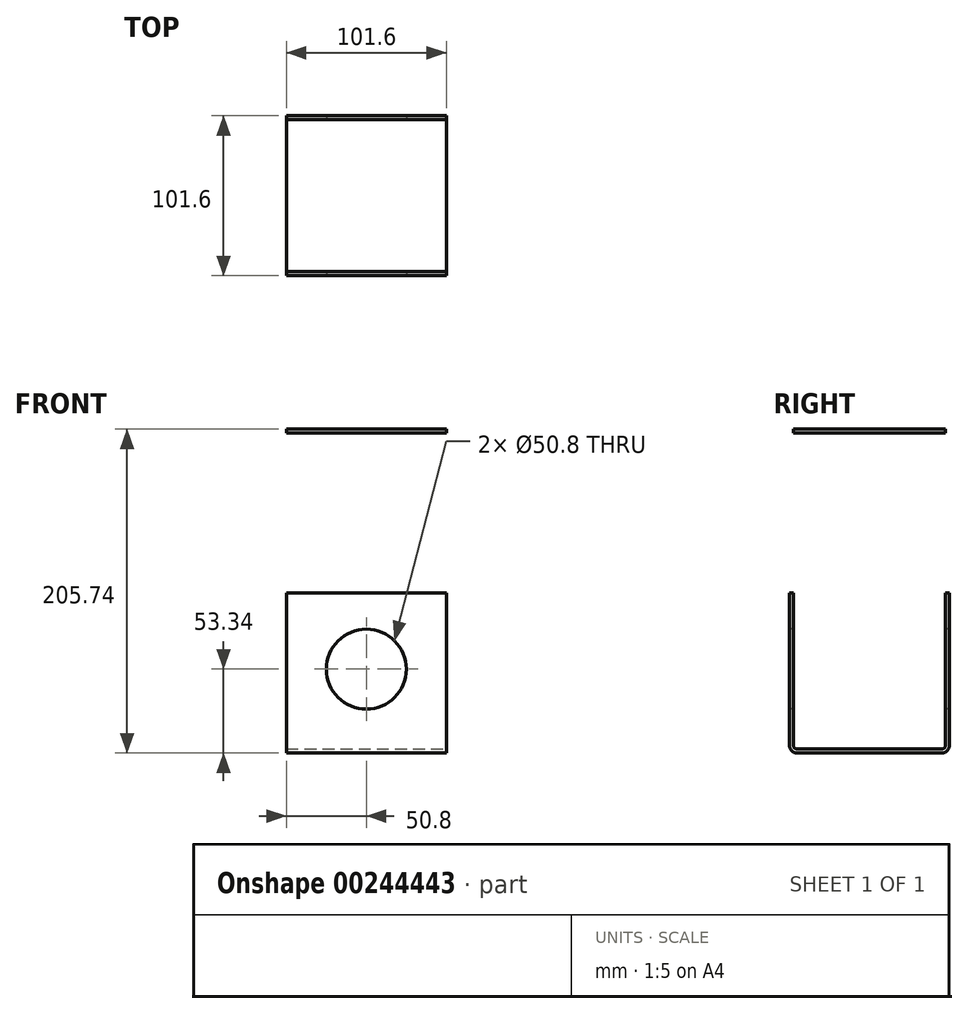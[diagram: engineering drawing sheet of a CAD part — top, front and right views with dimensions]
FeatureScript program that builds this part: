
annotation { "Feature Type Name" : "Feature", "Feature Type Description" : "" }
export const myFeature = defineFeature(function(context is Context, id is Id, definition is map)
    precondition{}
    {
        {
            var Q0;
            Q0=qCreatedBy(makeId("Top.planeOp"),FACE);
            var sketch = newSketch(context, id + "F0", { "sketchPlane" : qUnion([Q0])});
            skLineSegment(sketch, "E0.bottom", {"start": v(50.8, 50.8) * mm, "end": v(-50.8, 50.8) * mm});
            skLineSegment(sketch, "E0.top", {"start": v(50.8, -50.8) * mm, "end": v(-50.8, -50.8) * mm});
            skLineSegment(sketch, "E0.left", {"start": v(50.8, 50.8) * mm, "end": v(50.8, -50.8) * mm});
            skLineSegment(sketch, "E0.right", {"start": v(-50.8, 50.8) * mm, "end": v(-50.8, -50.8) * mm});
            skPoint(sketch, "E0.middle", {"position": v(0, 0) * mm});
            skSolve(sketch);
        }
        {
            var Q0;
            Q0 = qSketchRegion(id + "F0", true);
            extrude(context, id + "F1", {"entities" : qUnion([Q0]), "depth" : 101.6 * mm});
        }
        {
            var Q0;
            Q0=makeQuery(id+"F1.opExtrude","CAP_EDGE",EDGE,{"disambiguationData":[OSD([sQuery(id+"F0.wireOp",EDGE,"E0.top")])],"isStart":true});
            var Q1;
            Q1=makeQuery(id+"F1.opExtrude","CAP_EDGE",EDGE,{"disambiguationData":[OSD([sQuery(id+"F0.wireOp",EDGE,"E0.bottom")])],"isStart":true});
            fillet(context, id + "F2", {"entities" : qUnion([Q0, Q1]), "radius" : 5.08 * mm, "tangentPropagation" : true, "allowEdgeOverflow" : false});
        }
        {
            var Q0;
            Q0=makeQuery(id+"F1.opExtrude","CAP_FACE",FACE,{"disambiguationData":[OSD([sQuery(id+"F0.wireOp",EDGE,"E0.bottom"),sQuery(id+"F0.wireOp",EDGE,"E0.top"),sQuery(id+"F0.wireOp",EDGE,"E0.left"),sQuery(id+"F0.wireOp",EDGE,"E0.right")])],"isStart":false});
            var Q1;
            Q1=makeQuery(id+"F1.opExtrude","SWEPT_FACE",FACE,{"disambiguationData":[OSD([sQuery(id+"F0.wireOp",EDGE,"E0.right")])]});
            var Q2;
            Q2=makeQuery(id+"F1.opExtrude","SWEPT_FACE",FACE,{"disambiguationData":[OSD([sQuery(id+"F0.wireOp",EDGE,"E0.left")])]});
            shell(context, id + "F3", {"entities" : qUnion([Q0, Q1, Q2]), "thickness" : 2.54 * mm});
        }
        {
            var Q0;
            Q0=makeQuery(id+"F1.opExtrude","SWEPT_FACE",FACE,{"disambiguationData":[OSD([sQuery(id+"F0.wireOp",EDGE,"E0.top")])]});
            var sketch = newSketch(context, id + "F4", { "sketchPlane" : qUnion([Q0])});
            skLineSegment(sketch, "E1", {"start": v(-50.8, 53.34) * mm, "end": v(50.8, 53.34) * mm, "construction": true});
            skCircle(sketch, "E2", {"center": v(0, 53.34) * mm, "radius": 25.4 * mm});
            skSolve(sketch);
        }
        {
            var Q0;
            Q0 = qSketchRegion(id + "F4", true);
            extrude(context, id + "F5", {"entities" : qUnion([Q0]), "operationType" : NewBodyOperationType.REMOVE, "endBound" : BoundingType.THROUGH_ALL, "oppositeDirection" : true, "depth" : 25.4 * mm});
        }
        {
            var Q0;
            Q0=makeQuery(id+"F1.opExtrude","CAP_FACE",FACE,{"disambiguationData":[OSD([sQuery(id+"F0.wireOp",EDGE,"E0.bottom"),sQuery(id+"F0.wireOp",EDGE,"E0.top"),sQuery(id+"F0.wireOp",EDGE,"E0.left"),sQuery(id+"F0.wireOp",EDGE,"E0.right")])],"isStart":false});
            cPlane(context, id + "F6", {"entities" : qUnion([Q0]), "cplaneType" : CPlaneType.OFFSET, "offset" : 101.6 * mm, "width" : 152.4 * mm, "height" : 152.4 * mm});
        }
        {
            var Q0;
            Q0=qCreatedBy(id+"F6.planeOp",FACE);
            var sketch = newSketch(context, id + "F7", { "sketchPlane" : qUnion([Q0])});
            skLineSegment(sketch, "E3.0", {"start": v(-50.8, 45.72) * mm, "end": v(-50.8, -45.72) * mm});
            skLineSegment(sketch, "E3.1", {"start": v(50.8, 45.72) * mm, "end": v(50.8, -45.72) * mm});
            skLineSegment(sketch, "E3.2", {"start": v(50.8, 48.26) * mm, "end": v(-50.8, 48.26) * mm});
            skLineSegment(sketch, "E3.3", {"start": v(50.8, -48.26) * mm, "end": v(-50.8, -48.26) * mm});
            skLineSegment(sketch, "E4", {"start": v(-50.8, 45.72) * mm, "end": v(-50.8, 48.26) * mm});
            skLineSegment(sketch, "E5", {"start": v(50.8, 48.26) * mm, "end": v(50.8, 45.72) * mm});
            skLineSegment(sketch, "E6", {"start": v(50.8, -45.72) * mm, "end": v(50.8, -48.26) * mm});
            skLineSegment(sketch, "E7", {"start": v(-50.8, -45.72) * mm, "end": v(-50.8, -48.26) * mm});
            skSolve(sketch);
        }
        {
            var Q0;
            Q0 = qSketchRegion(id + "F7", true);
            extrude(context, id + "F8", {"entities" : qUnion([Q0]), "depth" : 2.54 * mm});
        }
    });
